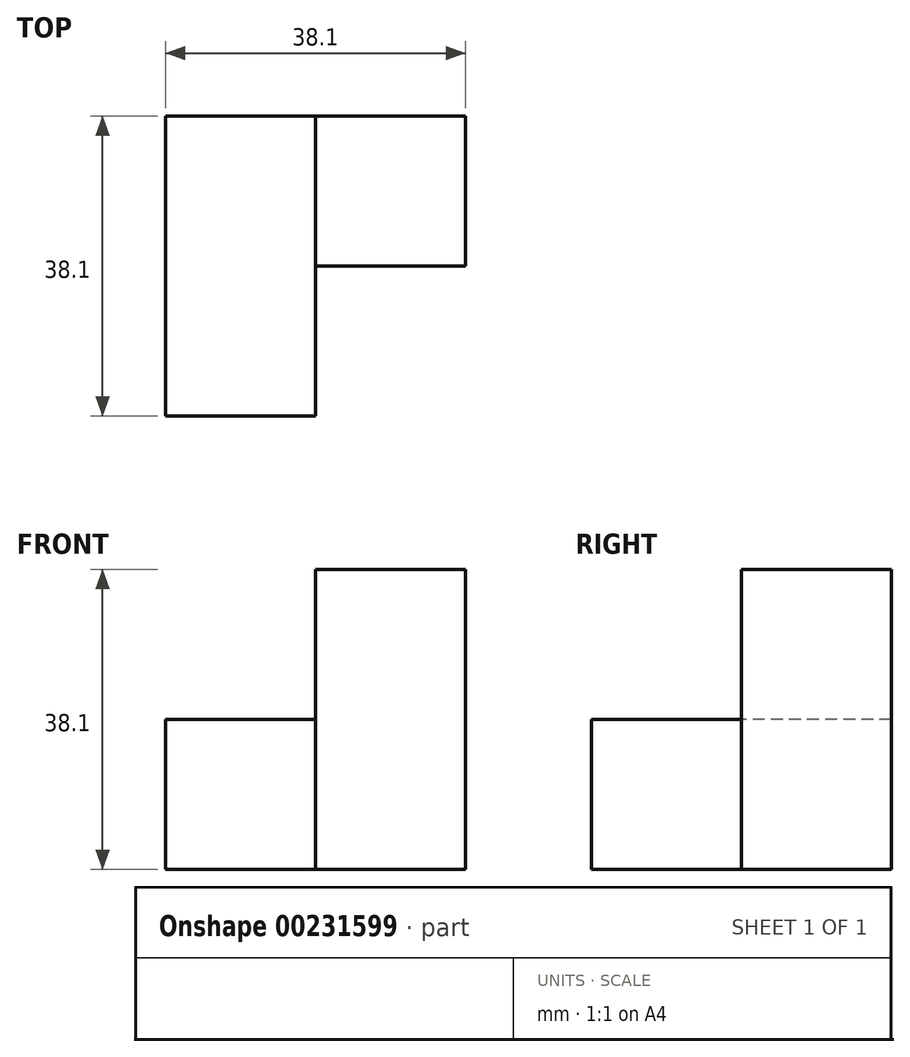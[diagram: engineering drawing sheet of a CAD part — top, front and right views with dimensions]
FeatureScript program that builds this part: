
annotation { "Feature Type Name" : "Feature", "Feature Type Description" : "" }
export const myFeature = defineFeature(function(context is Context, id is Id, definition is map)
    precondition{}
    {
        {
            var Q0;
            Q0=qCreatedBy(makeId("Front.planeOp"),FACE);
            var sketch = newSketch(context, id + "F0", { "sketchPlane" : qUnion([Q0])});
            skLineSegment(sketch, "E0.bottom", {"start": v(-24.77, 24.37) * mm, "end": v(-5.72, 24.37) * mm});
            skLineSegment(sketch, "E0.top", {"start": v(-24.77, -13.73) * mm, "end": v(-5.72, -13.73) * mm});
            skLineSegment(sketch, "E0.left", {"start": v(-24.77, 24.37) * mm, "end": v(-24.77, -13.73) * mm});
            skLineSegment(sketch, "E0.right", {"start": v(-5.72, 24.37) * mm, "end": v(-5.72, -13.73) * mm});
            skSolve(sketch);
        }
        {
            var Q0;
            Q0 = qSketchRegion(id + "F0", true);
            extrude(context, id + "F1", {"entities" : qUnion([Q0]), "depth" : 19.05 * mm});
        }
        {
            var Q0;
            Q0=makeQuery(id+"F1.opExtrude","SWEPT_FACE",FACE,{"disambiguationData":[OSD([sQuery(id+"F0.wireOp",EDGE,"E0.left")])]});
            var sketch = newSketch(context, id + "F2", { "sketchPlane" : qUnion([Q0])});
            skLineSegment(sketch, "E1.bottom", {"start": v(0, 5.32) * mm, "end": v(38.1, 5.32) * mm});
            skLineSegment(sketch, "E1.top", {"start": v(0, -13.73) * mm, "end": v(38.1, -13.73) * mm});
            skLineSegment(sketch, "E1.left", {"start": v(0, 5.32) * mm, "end": v(0, -13.73) * mm});
            skLineSegment(sketch, "E1.right", {"start": v(38.1, 5.32) * mm, "end": v(38.1, -13.73) * mm});
            skSolve(sketch);
        }
        {
            var Q0;
            {var subQ0=sQuery(id+"F2.wireOp",EDGE,"E1.left");Q0=makeQuery(id+"F2.imprint","IMPRINT",FACE,{"disambiguationData":[TD([[makeQuery(id+"F2.imprint","IMPRINT",EDGE,{"derivedFrom":subQ0}),1.0]])]});}
            var Q1;
            {var subQ0=sQuery(id+"F2.wireOp",EDGE,"E1.right");Q1=makeQuery(id+"F2.imprint","IMPRINT",FACE,{"disambiguationData":[TD([[makeQuery(id+"F2.imprint","IMPRINT",EDGE,{"derivedFrom":subQ0}),-1.0]])]});}
            extrude(context, id + "F3", {"entities" : qUnion([Q0, Q1]), "operationType" : NewBodyOperationType.ADD, "depth" : 19.05 * mm});
        }
    });
